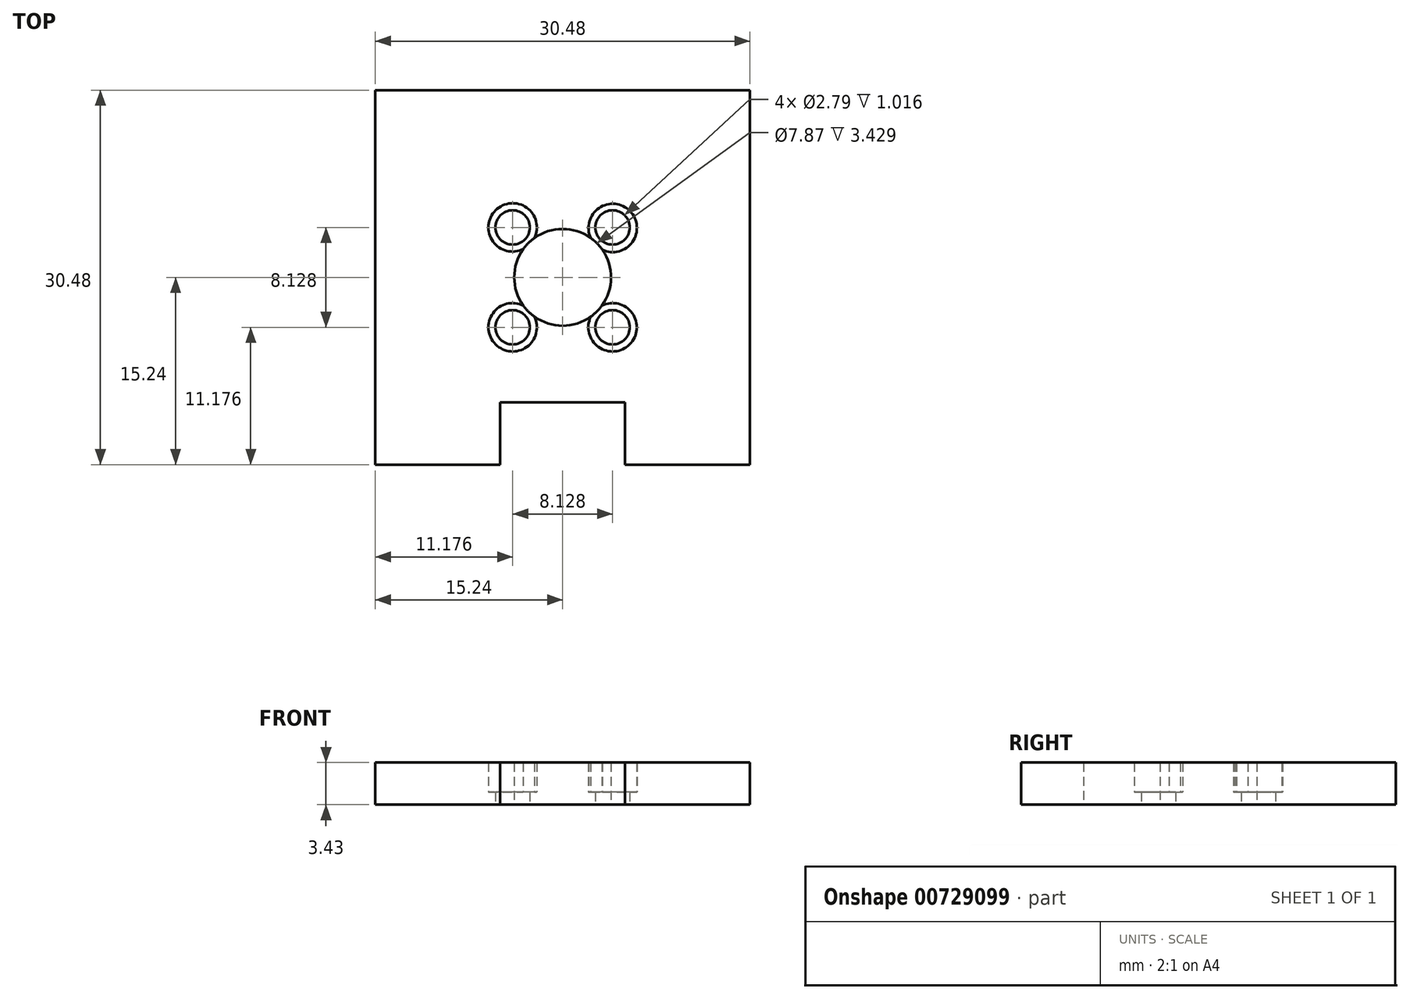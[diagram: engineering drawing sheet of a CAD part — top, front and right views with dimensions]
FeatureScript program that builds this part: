
annotation { "Feature Type Name" : "Feature", "Feature Type Description" : "" }
export const myFeature = defineFeature(function(context is Context, id is Id, definition is map)
    precondition{}
    {
        {
            var Q0;
            Q0=qCreatedBy(makeId("Top.planeOp"),FACE);
            var sketch = newSketch(context, id + "F0", { "sketchPlane" : qUnion([Q0])});
            skLineSegment(sketch, "E0.top", {"start": v(15.24, 15.24) * mm, "end": v(-15.24, 15.24) * mm});
            skLineSegment(sketch, "E0.left", {"start": v(15.24, -15.24) * mm, "end": v(15.24, 15.24) * mm});
            skLineSegment(sketch, "E0.right", {"start": v(-15.24, -15.24) * mm, "end": v(-15.24, 15.24) * mm});
            skPoint(sketch, "E0.middle", {"position": v(0, 0) * mm});
            skLineSegment(sketch, "E1", {"start": v(-15.24, -15.24) * mm, "end": v(-5.08, -15.24) * mm, "construction": true});
            skLineSegment(sketch, "E2", {"start": v(15.24, -15.24) * mm, "end": v(5.08, -15.24) * mm, "construction": true});
            skLineSegment(sketch, "E3", {"start": v(-5.08, -15.24) * mm, "end": v(-5.08, -10.16) * mm});
            skLineSegment(sketch, "E4", {"start": v(-5.08, -10.16) * mm, "end": v(5.08, -10.16) * mm});
            skLineSegment(sketch, "E5", {"start": v(5.08, -10.16) * mm, "end": v(5.08, -15.24) * mm});
            skLineSegment(sketch, "E6", {"start": v(-5.08, -15.24) * mm, "end": v(-15.24, -15.24) * mm});
            skLineSegment(sketch, "E7", {"start": v(5.08, -15.24) * mm, "end": v(15.24, -15.24) * mm});
            skCircle(sketch, "E8", {"center": v(0, 0) * mm, "radius": 3.94 * mm});
            skCircle(sketch, "E9", {"center": v(-4.06, 4.06) * mm, "radius": 1.4 * mm});
            skCircle(sketch, "E10", {"center": v(4.06, 4.06) * mm, "radius": 1.4 * mm});
            skCircle(sketch, "E11", {"center": v(4.06, -4.06) * mm, "radius": 1.4 * mm});
            skCircle(sketch, "E12", {"center": v(-4.06, -4.06) * mm, "radius": 1.4 * mm});
            skPoint(sketch, "E13.orphan", {"position": v(2.78, -2.78) * mm});
            skCircle(sketch, "E14", {"center": v(-4.06, 4.06) * mm, "radius": 1.97 * mm});
            skCircle(sketch, "E15", {"center": v(4.07, 4.01) * mm, "radius": 1.97 * mm});
            skCircle(sketch, "E16", {"center": v(-4.06, -4.06) * mm, "radius": 1.97 * mm});
            skCircle(sketch, "E17", {"center": v(4.06, -4.06) * mm, "radius": 1.97 * mm});
            skSolve(sketch);
        }
        {
            var Q0;
            Q0=makeQuery(id+"F0.imprint","IMPRINT",FACE,{"disambiguationData":[TD([[makeQuery(id+"F0.imprint","IMPRINT",EDGE,{"derivedFrom":sQuery(id+"F0.wireOp",EDGE,"E0.top")}),1.0]])]});
            extrude(context, id + "F1", {"entities" : qUnion([Q0]), "depth" : 3.43 * mm, "offsetDistance" : 25.4 * mm});
        }
        {
            var Q0;
            Q0=makeQuery(id+"F0.imprint","IMPRINT",FACE,{"disambiguationData":[TD([[makeQuery(id+"F0.imprint","IMPRINT",EDGE,{"derivedFrom":sQuery(id+"F0.wireOp",EDGE,"E9")}),-1.0]])]});
            var Q1;
            Q1=makeQuery(id+"F0.imprint","IMPRINT",FACE,{"disambiguationData":[TD([[makeQuery(id+"F0.imprint","IMPRINT",EDGE,{"derivedFrom":sQuery(id+"F0.wireOp",EDGE,"E10")}),-1.0]])]});
            var Q2;
            Q2=makeQuery(id+"F0.imprint","IMPRINT",FACE,{"disambiguationData":[TD([[makeQuery(id+"F0.imprint","IMPRINT",EDGE,{"derivedFrom":sQuery(id+"F0.wireOp",EDGE,"E12")}),-1.0]])]});
            var Q3;
            Q3=makeQuery(id+"F0.imprint","IMPRINT",FACE,{"disambiguationData":[TD([[makeQuery(id+"F0.imprint","IMPRINT",EDGE,{"derivedFrom":sQuery(id+"F0.wireOp",EDGE,"E11")}),-1.0]])]});
            extrude(context, id + "F2", {"entities" : qUnion([Q0, Q1, Q2, Q3]), "operationType" : NewBodyOperationType.ADD, "depth" : 3.05 * mm, "offsetDistance" : 25.4 * mm});
        }
        {
            var Q0;
            Q0=makeQuery(id+"F2.opExtrude","CAP_FACE",FACE,{"disambiguationData":[OSD([sQuery(id+"F0.wireOp",EDGE,"E8"),sQuery(id+"F0.wireOp",EDGE,"E9"),sQuery(id+"F0.wireOp",EDGE,"E14")])],"isStart":false});
            var Q1;
            Q1=makeQuery(id+"F2.opExtrude","CAP_FACE",FACE,{"disambiguationData":[OSD([sQuery(id+"F0.wireOp",EDGE,"E8"),sQuery(id+"F0.wireOp",EDGE,"E12"),sQuery(id+"F0.wireOp",EDGE,"E16")])],"isStart":false});
            var Q2;
            Q2=makeQuery(id+"F2.opExtrude","CAP_FACE",FACE,{"disambiguationData":[OSD([sQuery(id+"F0.wireOp",EDGE,"E8"),sQuery(id+"F0.wireOp",EDGE,"E10"),sQuery(id+"F0.wireOp",EDGE,"E15")])],"isStart":false});
            var Q3;
            Q3=makeQuery(id+"F2.opExtrude","CAP_FACE",FACE,{"disambiguationData":[OSD([sQuery(id+"F0.wireOp",EDGE,"E8"),sQuery(id+"F0.wireOp",EDGE,"E11"),sQuery(id+"F0.wireOp",EDGE,"E17")])],"isStart":false});
            extrude(context, id + "F3", {"entities" : qUnion([Q0, Q1, Q2, Q3]), "operationType" : NewBodyOperationType.REMOVE, "oppositeDirection" : true, "depth" : 2.03 * mm, "offsetDistance" : 25.4 * mm});
        }
    });
